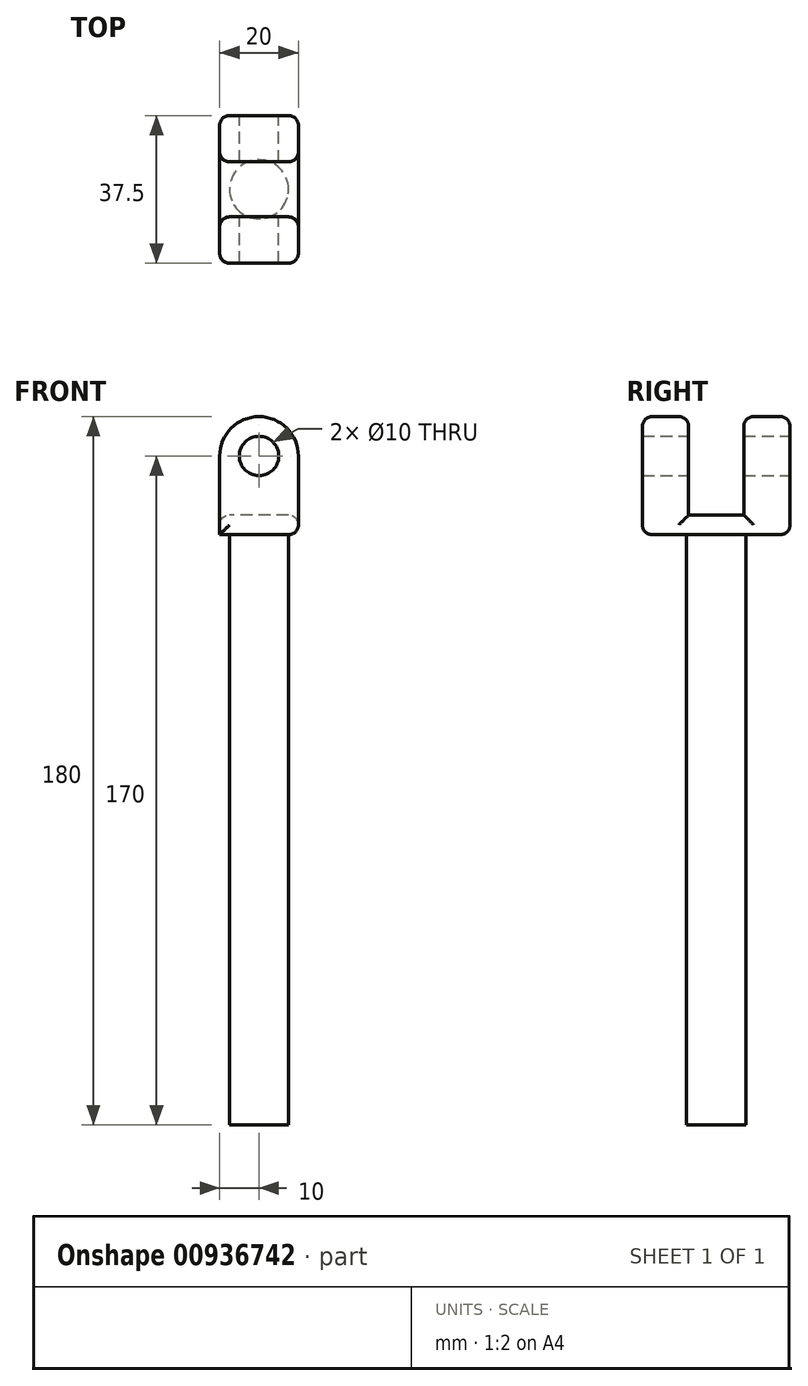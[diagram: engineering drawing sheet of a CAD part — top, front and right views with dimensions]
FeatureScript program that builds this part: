
annotation { "Feature Type Name" : "Feature", "Feature Type Description" : "" }
export const myFeature = defineFeature(function(context is Context, id is Id, definition is map)
    precondition{}
    {
        {
            var Q0;
            Q0=qCreatedBy(makeId("Front.planeOp"),FACE);
            var sketch = newSketch(context, id + "F0", { "sketchPlane" : qUnion([Q0])});
            skCircle(sketch, "E0", {"center": v(0, 20) * mm, "radius": 5 * mm});
            skArc(sketch, "E1", {"start": v(10, 20) * mm, "mid": v(0, 30) * mm, "end": v(-10, 20) * mm});
            skLineSegment(sketch, "E2", {"start": v(10, 20) * mm, "end": v(10, 0) * mm});
            skLineSegment(sketch, "E3", {"start": v(-10, 20) * mm, "end": v(-10, 0) * mm});
            skLineSegment(sketch, "E4", {"start": v(-10, 0) * mm, "end": v(10, 0) * mm});
            skSolve(sketch);
        }
        {
            var Q0;
            Q0=makeQuery(id+"F0.imprint","IMPRINT",FACE,{"disambiguationData":[TD([[makeQuery(id+"F0.imprint","IMPRINT",EDGE,{"derivedFrom":sQuery(id+"F0.wireOp",EDGE,"E0")}),-1.0]])]});
            extrude(context, id + "F1", {"entities" : qUnion([Q0]), "depth" : 18.75 * mm, "offsetDistance" : 25 * mm, "hasSecondDirection" : true, "secondDirectionOppositeDirection" : true, "secondDirectionDepth" : 18.75 * mm});
        }
        {
            var Q0;
            Q0=makeQuery(id+"F1.opExtrude","CAP_FACE",FACE,{"disambiguationData":[OSD([sQuery(id+"F0.wireOp",EDGE,"E0"),sQuery(id+"F0.wireOp",EDGE,"E1"),sQuery(id+"F0.wireOp",EDGE,"E2"),sQuery(id+"F0.wireOp",EDGE,"E3"),sQuery(id+"F0.wireOp",EDGE,"E4")])],"isStart":false});
            cPlane(context, id + "F2", {"entities" : qUnion([Q0]), "cplaneType" : CPlaneType.OFFSET, "offset" : 18.75 * mm, "oppositeDirection" : true, "width" : 150 * mm, "height" : 150 * mm});
        }
        {
            var Q0;
            Q0=qCreatedBy(id+"F2.planeOp",FACE);
            var sketch = newSketch(context, id + "F3", { "sketchPlane" : qUnion([Q0])});
            skLineSegment(sketch, "E5", {"start": v(0, 5) * mm, "end": v(12, 5) * mm});
            skLineSegment(sketch, "E6", {"start": v(12, 5) * mm, "end": v(12, 35) * mm});
            skLineSegment(sketch, "E7", {"start": v(12, 35) * mm, "end": v(-12, 35) * mm});
            skLineSegment(sketch, "E8", {"start": v(0, 5) * mm, "end": v(-12, 5) * mm});
            skLineSegment(sketch, "E9", {"start": v(-12, 5) * mm, "end": v(-12, 35) * mm});
            skSolve(sketch);
        }
        {
            var Q0;
            Q0=makeQuery(id+"F3.imprint","IMPRINT",FACE,{"disambiguationData":[TD([[makeQuery(id+"F3.imprint","IMPRINT",EDGE,{"derivedFrom":sQuery(id+"F3.wireOp",EDGE,"E5")}),1.0]])]});
            extrude(context, id + "F4", {"entities" : qUnion([Q0]), "operationType" : NewBodyOperationType.REMOVE, "oppositeDirection" : true, "depth" : 7 * mm, "offsetDistance" : 25 * mm, "hasSecondDirection" : true, "secondDirectionOppositeDirection" : false, "secondDirectionDepth" : 7 * mm});
        }
        {
            var Q0;
            Q0=makeQuery(id+"F1.opExtrude","SWEPT_FACE",FACE,{"disambiguationData":[OSD([sQuery(id+"F0.wireOp",EDGE,"E4")])]});
            cPlane(context, id + "F5", {"entities" : qUnion([Q0]), "cplaneType" : CPlaneType.OFFSET, "offset" : 0 * mm, "width" : 150 * mm, "height" : 150 * mm});
        }
        {
            var Q0;
            Q0=qCreatedBy(id+"F5.planeOp",FACE);
            var sketch = newSketch(context, id + "F6", { "sketchPlane" : qUnion([Q0])});
            skCircle(sketch, "E10", {"center": v(0, 0) * mm, "radius": 7.5 * mm});
            skSolve(sketch);
        }
        {
            var Q0;
            Q0=makeQuery(id+"F6.imprint","IMPRINT",FACE,{"disambiguationData":[TD([[makeQuery(id+"F6.imprint","IMPRINT",EDGE,{"derivedFrom":sQuery(id+"F6.wireOp",EDGE,"ffAmSKi8-vrYt-WQpH-TePC-HCcZlY9Wo8Om")}),1.0]])]});
            var Q1;
            Q1=makeQuery(id+"F6.imprint","IMPRINT",FACE,{"disambiguationData":[TD([[makeQuery(id+"F6.imprint","IMPRINT",EDGE,{"derivedFrom":sQuery(id+"F6.wireOp",EDGE,"E10")}),1.0]])]});
            extrude(context, id + "F7", {"entities" : qUnion([Q0, Q1]), "operationType" : NewBodyOperationType.ADD, "depth" : 150 * mm, "offsetDistance" : 25 * mm});
        }
        {
            var Q0;
            Q0=makeQuery(id+"F4.boolean.opBoolean","INTERSECT",EDGE,{"derivedFrom":[makeQuery(id+"F1.opExtrude","SWEPT_FACE",FACE,{"disambiguationData":[OSD([sQuery(id+"F0.wireOp",EDGE,"E2")])]}),makeQuery(id+"F4.opExtrude","CAP_FACE",FACE,{"disambiguationData":[OSD([sQuery(id+"F3.wireOp",EDGE,"E5"),sQuery(id+"F3.wireOp",EDGE,"E6"),sQuery(id+"F3.wireOp",EDGE,"E7"),sQuery(id+"F3.wireOp",EDGE,"E8"),sQuery(id+"F3.wireOp",EDGE,"E9")])],"isStart":true})]});
            var Q1;
            Q1=makeQuery(id+"F4.boolean.opBoolean","INTERSECT",EDGE,{"derivedFrom":[makeQuery(id+"F1.opExtrude","SWEPT_FACE",FACE,{"disambiguationData":[OSD([sQuery(id+"F0.wireOp",EDGE,"E2")])]}),makeQuery(id+"F4.opExtrude","CAP_FACE",FACE,{"disambiguationData":[OSD([sQuery(id+"F3.wireOp",EDGE,"E5"),sQuery(id+"F3.wireOp",EDGE,"E6"),sQuery(id+"F3.wireOp",EDGE,"E7"),sQuery(id+"F3.wireOp",EDGE,"E8"),sQuery(id+"F3.wireOp",EDGE,"E9")])],"isStart":false})]});
            var Q2;
            Q2=makeQuery(id+"F1.opExtrude","CAP_EDGE",EDGE,{"disambiguationData":[OSD([sQuery(id+"F0.wireOp",EDGE,"E2")])],"isStart":true});
            var Q3;
            Q3=makeQuery(id+"F1.opExtrude","CAP_EDGE",EDGE,{"disambiguationData":[OSD([sQuery(id+"F0.wireOp",EDGE,"E2")])],"isStart":false});
            var Q4;
            Q4=makeQuery(id+"F4.boolean.opBoolean","INTERSECT",EDGE,{"derivedFrom":[makeQuery(id+"F1.opExtrude","SWEPT_FACE",FACE,{"disambiguationData":[OSD([sQuery(id+"F0.wireOp",EDGE,"E2")])]}),makeQuery(id+"F4.opExtrude","SWEPT_FACE",FACE,{"disambiguationData":[OSD([sQuery(id+"F3.wireOp",EDGE,"E5"),sQuery(id+"F3.wireOp",EDGE,"E8")])]})]});
            var Q5;
            Q5=makeQuery(id+"F4.boolean.opBoolean","INTERSECT",EDGE,{"derivedFrom":[makeQuery(id+"F1.opExtrude","SWEPT_FACE",FACE,{"disambiguationData":[OSD([sQuery(id+"F0.wireOp",EDGE,"E3")])]}),makeQuery(id+"F4.opExtrude","SWEPT_FACE",FACE,{"disambiguationData":[OSD([sQuery(id+"F3.wireOp",EDGE,"E5"),sQuery(id+"F3.wireOp",EDGE,"E8")])]})]});
            var Q6;
            {var subQ0=sQuery(id+"F0.wireOp",EDGE,"E4");var subQ1=sQuery(id+"F0.wireOp",EDGE,"E2");Q6=makeQuery(id+"F7.boolean.opBoolean","SPLIT",EDGE,{"disambiguationData":[TD([makeQuery(id+"F1.opExtrude","CAP_FACE",FACE,{"disambiguationData":[OSD([sQuery(id+"F0.wireOp",EDGE,"E0"),sQuery(id+"F0.wireOp",EDGE,"E1"),subQ1,sQuery(id+"F0.wireOp",EDGE,"E3"),subQ0])],"isStart":true})])],"derivedFrom":makeQuery(id+"F1.opExtrude","SWEPT_EDGE",EDGE,{"disambiguationData":[OSD([subQ1,subQ0])]})});}
            var Q7;
            Q7=makeQuery(id+"F1.opExtrude","CAP_EDGE",EDGE,{"disambiguationData":[OSD([sQuery(id+"F0.wireOp",EDGE,"E4")])],"isStart":true});
            var Q8;
            Q8=makeQuery(id+"F1.opExtrude","CAP_EDGE",EDGE,{"disambiguationData":[OSD([sQuery(id+"F0.wireOp",EDGE,"E4")])],"isStart":false});
            fillet(context, id + "F8", {"entities" : qUnion([Q0, Q1, Q2, Q3, Q4, Q5, Q6, Q7, Q8]), "radius" : 2.5 * mm, "tangentPropagation" : true, "allowEdgeOverflow" : false});
        }
    });
